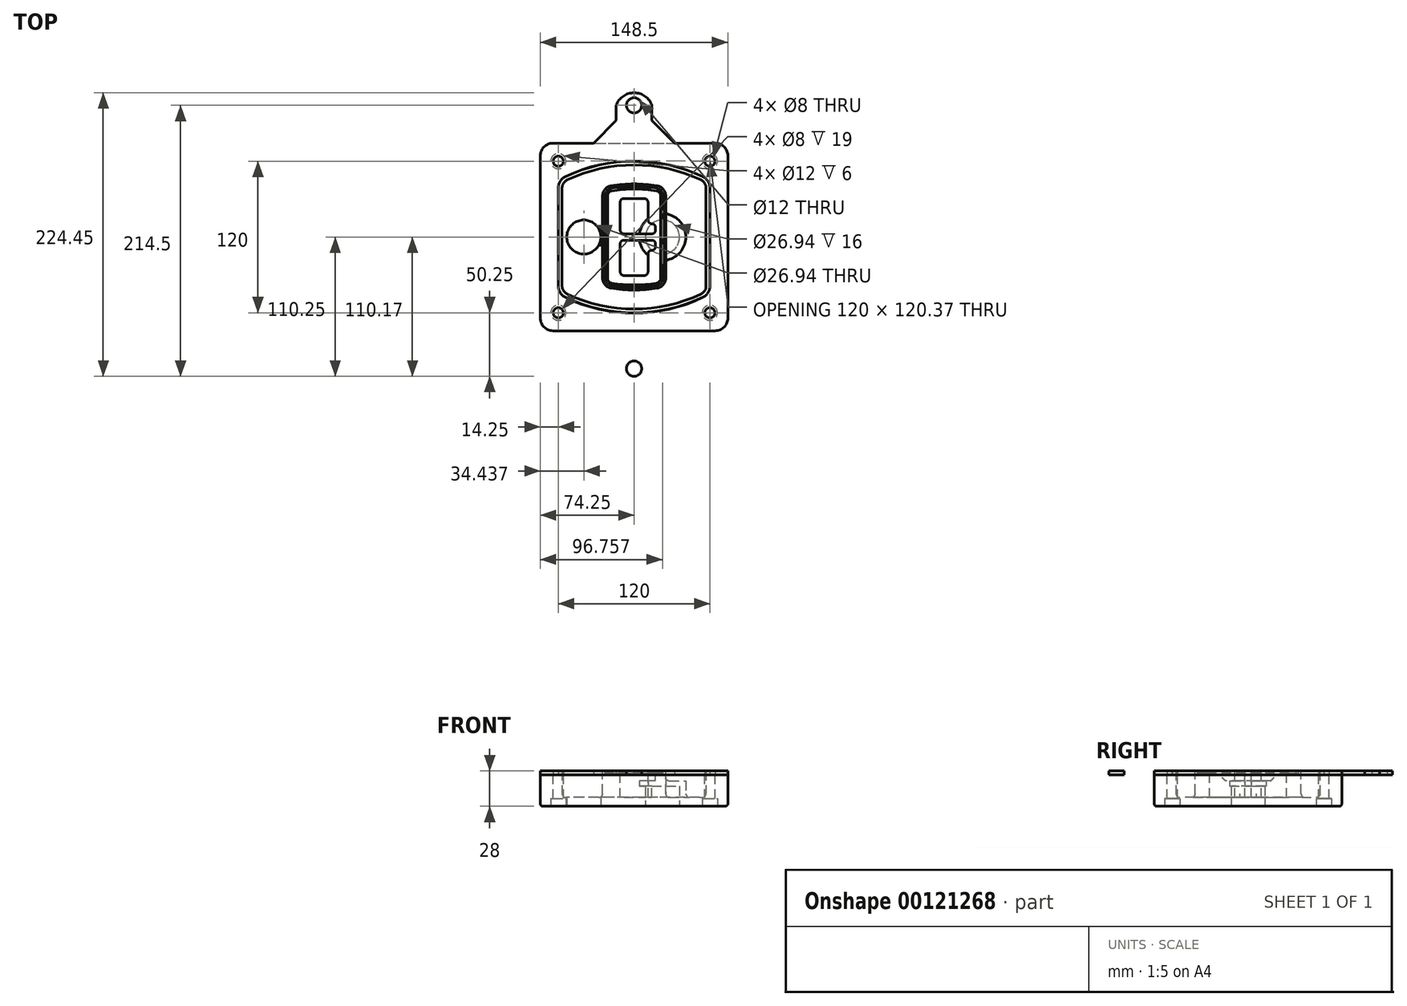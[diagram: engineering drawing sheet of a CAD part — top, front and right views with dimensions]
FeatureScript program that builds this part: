
annotation { "Feature Type Name" : "Feature", "Feature Type Description" : "" }
export const myFeature = defineFeature(function(context is Context, id is Id, definition is map)
    precondition{}
    {
        {
            var Q0;
            Q0=qCreatedBy(makeId("Top.planeOp"),FACE);
            var sketch = newSketch(context, id + "F0", { "sketchPlane" : qUnion([Q0])});
            skPoint(sketch, "E0.rect.middle", {"position": v(0, 0) * mm});
            skLineSegment(sketch, "E1.bottom", {"start": v(-64.25, -74.25) * mm, "end": v(64.25, -74.25) * mm});
            skLineSegment(sketch, "E1.top", {"start": v(-64.25, 74.25) * mm, "end": v(64.25, 74.25) * mm});
            skLineSegment(sketch, "E1.left", {"start": v(-74.25, -64.25) * mm, "end": v(-74.25, 64.25) * mm});
            skLineSegment(sketch, "E1.right", {"start": v(74.25, -64.25) * mm, "end": v(74.25, 64.25) * mm});
            skLineSegment(sketch, "E2", {"start": v(-74.25, 74.25) * mm, "end": v(74.25, -74.25) * mm, "construction": true});
            skLineSegment(sketch, "E3", {"start": v(74.25, 74.25) * mm, "end": v(-74.25, -74.25) * mm, "construction": true});
            skCircle(sketch, "E4", {"center": v(-60, 60) * mm, "radius": 4 * mm});
            skCircle(sketch, "E5", {"center": v(60, 60) * mm, "radius": 4 * mm});
            skCircle(sketch, "E6", {"center": v(60, -60) * mm, "radius": 4 * mm});
            skCircle(sketch, "E7", {"center": v(-60, -60) * mm, "radius": 4 * mm});
            skLineSegment(sketch, "E8", {"start": v(-60, 60) * mm, "end": v(60, 60) * mm, "construction": true});
            skLineSegment(sketch, "E9", {"start": v(60, 60) * mm, "end": v(60, -60) * mm, "construction": true});
            skLineSegment(sketch, "E10", {"start": v(60, -60) * mm, "end": v(-60, -60) * mm, "construction": true});
            skLineSegment(sketch, "E11", {"start": v(-60, -60) * mm, "end": v(-60, 60) * mm, "construction": true});
            skLineSegment(sketch, "E12", {"start": v(-60, 38.83) * mm, "end": v(-60, -38.83) * mm});
            skLineSegment(sketch, "E13", {"start": v(60, 38.83) * mm, "end": v(60, -38.83) * mm});
            skArc(sketch, "E14", {"start": v(54.26, 47.88) * mm, "mid": v(0, 60) * mm, "end": v(-54.26, 47.88) * mm});
            skArc(sketch, "E15", {"start": v(-54.26, -47.88) * mm, "mid": v(0, -60) * mm, "end": v(54.26, -47.88) * mm});
            skLineSegment(sketch, "E16", {"start": v(-60, 0) * mm, "end": v(60, 0) * mm, "construction": true});
            skPoint(sketch, "E17.visualSharp", {"position": v(-60, -45) * mm});
            skArc(sketch, "E17.filletArc", {"start": v(-60, -38.83) * mm, "mid": v(-58.44, -44.2) * mm, "end": v(-54.26, -47.88) * mm});
            skPoint(sketch, "E18.visualSharp", {"position": v(-60, 45) * mm});
            skArc(sketch, "E18.filletArc", {"start": v(-54.26, 47.88) * mm, "mid": v(-58.44, 44.2) * mm, "end": v(-60, 38.83) * mm});
            skPoint(sketch, "E19.visualSharp", {"position": v(60, 45) * mm});
            skArc(sketch, "E19.filletArc", {"start": v(60, 38.83) * mm, "mid": v(58.44, 44.2) * mm, "end": v(54.26, 47.88) * mm});
            skPoint(sketch, "E20.visualSharp", {"position": v(60, -45) * mm});
            skArc(sketch, "E20.filletArc", {"start": v(54.26, -47.88) * mm, "mid": v(58.44, -44.2) * mm, "end": v(60, -38.83) * mm});
            skPoint(sketch, "E21.visualSharp", {"position": v(-74.25, 74.25) * mm});
            skArc(sketch, "E21.filletArc", {"start": v(-64.25, 74.25) * mm, "mid": v(-71.32, 71.32) * mm, "end": v(-74.25, 64.25) * mm});
            skPoint(sketch, "E22.visualSharp", {"position": v(74.25, 74.25) * mm});
            skArc(sketch, "E22.filletArc", {"start": v(74.25, 64.25) * mm, "mid": v(71.32, 71.32) * mm, "end": v(64.25, 74.25) * mm});
            skPoint(sketch, "E23.visualSharp", {"position": v(74.25, -74.25) * mm});
            skArc(sketch, "E23.filletArc", {"start": v(64.25, -74.25) * mm, "mid": v(71.32, -71.32) * mm, "end": v(74.25, -64.25) * mm});
            skPoint(sketch, "E24.visualSharp", {"position": v(-74.25, -74.25) * mm});
            skArc(sketch, "E24.filletArc", {"start": v(-74.25, -64.25) * mm, "mid": v(-71.32, -71.32) * mm, "end": v(-64.25, -74.25) * mm});
            skArc(sketch, "E25.0", {"start": v(57, 38.83) * mm, "mid": v(55.9, 42.58) * mm, "end": v(52.98, 45.17) * mm});
            skLineSegment(sketch, "E25.1", {"start": v(57, 38.83) * mm, "end": v(57, -38.83) * mm});
            skArc(sketch, "E25.2", {"start": v(52.98, -45.17) * mm, "mid": v(55.9, -42.58) * mm, "end": v(57, -38.83) * mm});
            skArc(sketch, "E25.3", {"start": v(-52.98, -45.17) * mm, "mid": v(0, -57) * mm, "end": v(52.98, -45.17) * mm});
            skArc(sketch, "E25.4", {"start": v(-57, -38.83) * mm, "mid": v(-55.9, -42.58) * mm, "end": v(-52.98, -45.17) * mm});
            skArc(sketch, "E25.5", {"start": v(52.98, 45.17) * mm, "mid": v(0, 57) * mm, "end": v(-52.98, 45.17) * mm});
            skLineSegment(sketch, "E25.6", {"start": v(-57, 38.83) * mm, "end": v(-57, -38.83) * mm});
            skArc(sketch, "E25.7", {"start": v(-52.98, 45.17) * mm, "mid": v(-55.9, 42.58) * mm, "end": v(-57, 38.83) * mm});
            skArc(sketch, "E26.0", {"start": v(-55.96, 51.5) * mm, "mid": v(-61.82, 46.33) * mm, "end": v(-64, 38.83) * mm});
            skArc(sketch, "E26.1", {"start": v(55.96, 51.5) * mm, "mid": v(0, 64) * mm, "end": v(-55.96, 51.5) * mm});
            skArc(sketch, "E26.2", {"start": v(64, 38.83) * mm, "mid": v(61.82, 46.33) * mm, "end": v(55.96, 51.5) * mm});
            skLineSegment(sketch, "E26.3", {"start": v(64, 38.83) * mm, "end": v(64, -38.83) * mm});
            skArc(sketch, "E26.4", {"start": v(55.96, -51.5) * mm, "mid": v(61.82, -46.33) * mm, "end": v(64, -38.83) * mm});
            skLineSegment(sketch, "E26.5", {"start": v(-64, 38.83) * mm, "end": v(-64, -38.83) * mm});
            skArc(sketch, "E26.6", {"start": v(-55.96, -51.5) * mm, "mid": v(0, -64) * mm, "end": v(55.96, -51.5) * mm});
            skArc(sketch, "E26.7", {"start": v(-64, -38.83) * mm, "mid": v(-61.82, -46.33) * mm, "end": v(-55.96, -51.5) * mm});
            skSolve(sketch);
        }
        {
            var Q0;
            Q0=makeQuery(id+"F0.imprint","IMPRINT",FACE,{"disambiguationData":[TD([[makeQuery(id+"F0.imprint","IMPRINT",EDGE,{"derivedFrom":sQuery(id+"F0.wireOp",EDGE,"E1.bottom")}),1.0]])]});
            var Q1;
            Q1=makeQuery(id+"F0.imprint","IMPRINT",FACE,{"disambiguationData":[TD([[makeQuery(id+"F0.imprint","IMPRINT",EDGE,{"derivedFrom":sQuery(id+"F0.wireOp",EDGE,"E12")}),1.0]])]});
            var Q2;
            Q2=makeQuery(id+"F0.imprint","IMPRINT",FACE,{"disambiguationData":[TD([[makeQuery(id+"F0.imprint","IMPRINT",EDGE,{"derivedFrom":sQuery(id+"F0.wireOp",EDGE,"E25.0")}),1.0]])]});
            var Q3;
            Q3=makeQuery(id+"F0.imprint","IMPRINT",FACE,{"disambiguationData":[TD([[makeQuery(id+"F0.imprint","IMPRINT",EDGE,{"derivedFrom":sQuery(id+"F0.wireOp",EDGE,"E12")}),-1.0]])]});
            extrude(context, id + "F1", {"entities" : qUnion([Q0, Q1, Q2, Q3]), "oppositeDirection" : true, "depth" : 25 * mm});
        }
        {
            var Q0;
            Q0=makeQuery(id+"F0.imprint","IMPRINT",FACE,{"disambiguationData":[TD([[makeQuery(id+"F0.imprint","IMPRINT",EDGE,{"derivedFrom":sQuery(id+"F0.wireOp",EDGE,"E12")}),1.0]])]});
            extrude(context, id + "F2", {"entities" : qUnion([Q0]), "operationType" : NewBodyOperationType.ADD, "depth" : 3 * mm});
        }
        {
            var Q0;
            Q0=makeQuery(id+"F0.imprint","IMPRINT",FACE,{"disambiguationData":[TD([[makeQuery(id+"F0.imprint","IMPRINT",EDGE,{"derivedFrom":sQuery(id+"F0.wireOp",EDGE,"E25.0")}),1.0]])]});
            extrude(context, id + "F3", {"entities" : qUnion([Q0]), "operationType" : NewBodyOperationType.REMOVE, "oppositeDirection" : true, "depth" : 18 * mm});
        }
        {
            var Q0;
            Q0=makeQuery(id+"F2.opExtrude","CAP_FACE",FACE,{"disambiguationData":[OSD([sQuery(id+"F0.wireOp",EDGE,"E12"),sQuery(id+"F0.wireOp",EDGE,"E13"),sQuery(id+"F0.wireOp",EDGE,"E14"),sQuery(id+"F0.wireOp",EDGE,"E15"),sQuery(id+"F0.wireOp",EDGE,"E17.filletArc"),sQuery(id+"F0.wireOp",EDGE,"E18.filletArc"),sQuery(id+"F0.wireOp",EDGE,"E19.filletArc"),sQuery(id+"F0.wireOp",EDGE,"E20.filletArc"),sQuery(id+"F0.wireOp",EDGE,"E25.0"),sQuery(id+"F0.wireOp",EDGE,"E25.1"),sQuery(id+"F0.wireOp",EDGE,"E25.2"),sQuery(id+"F0.wireOp",EDGE,"E25.3"),sQuery(id+"F0.wireOp",EDGE,"E25.4"),sQuery(id+"F0.wireOp",EDGE,"E25.5"),sQuery(id+"F0.wireOp",EDGE,"E25.6"),sQuery(id+"F0.wireOp",EDGE,"E25.7")])],"isStart":false});
            var sketch = newSketch(context, id + "F4", { "sketchPlane" : qUnion([Q0])});
            skArc(sketch, "E27.0", {"start": v(-18.34, -40.45) * mm, "mid": v(0, -42) * mm, "end": v(18.34, -40.45) * mm});
            skArc(sketch, "E28.0", {"start": v(18.34, 40.45) * mm, "mid": v(0, 42) * mm, "end": v(-18.34, 40.45) * mm});
            skLineSegment(sketch, "E29", {"start": v(-25, 32.57) * mm, "end": v(-25, -32.57) * mm});
            skLineSegment(sketch, "E30", {"start": v(25, 32.57) * mm, "end": v(25, -32.57) * mm});
            skLineSegment(sketch, "E31", {"start": v(-25, 39.1) * mm, "end": v(25, 39.1) * mm, "construction": true});
            skLineSegment(sketch, "E32", {"start": v(-25, -39.1) * mm, "end": v(25, -39.1) * mm, "construction": true});
            skPoint(sketch, "E33.visualSharp", {"position": v(-25, 39.1) * mm});
            skArc(sketch, "E33.filletArc", {"start": v(-18.34, 40.45) * mm, "mid": v(-23.11, 37.73) * mm, "end": v(-25, 32.57) * mm});
            skPoint(sketch, "E34.visualSharp", {"position": v(25, 39.1) * mm});
            skArc(sketch, "E34.filletArc", {"start": v(25, 32.57) * mm, "mid": v(23.11, 37.73) * mm, "end": v(18.34, 40.45) * mm});
            skPoint(sketch, "E35.visualSharp", {"position": v(25, -39.1) * mm});
            skArc(sketch, "E35.filletArc", {"start": v(18.34, -40.45) * mm, "mid": v(23.11, -37.73) * mm, "end": v(25, -32.57) * mm});
            skPoint(sketch, "E36.visualSharp", {"position": v(-25, -39.1) * mm});
            skArc(sketch, "E36.filletArc", {"start": v(-25, -32.57) * mm, "mid": v(-23.11, -37.73) * mm, "end": v(-18.34, -40.45) * mm});
            skArc(sketch, "E37.0", {"start": v(52.98, 45.17) * mm, "mid": v(0, 57) * mm, "end": v(-52.98, 45.17) * mm});
            skArc(sketch, "E37.1", {"start": v(-52.98, 45.17) * mm, "mid": v(-55.9, 42.58) * mm, "end": v(-57, 38.83) * mm});
            skLineSegment(sketch, "E37.2", {"start": v(-57, 38.83) * mm, "end": v(-57, -38.83) * mm});
            skArc(sketch, "E37.3", {"start": v(-57, -38.83) * mm, "mid": v(-55.9, -42.58) * mm, "end": v(-52.98, -45.17) * mm});
            skArc(sketch, "E37.4", {"start": v(-52.98, -45.17) * mm, "mid": v(0, -57) * mm, "end": v(52.98, -45.17) * mm});
            skArc(sketch, "E37.5", {"start": v(52.98, -45.17) * mm, "mid": v(55.9, -42.58) * mm, "end": v(57, -38.83) * mm});
            skLineSegment(sketch, "E37.6", {"start": v(57, 38.83) * mm, "end": v(57, -38.83) * mm});
            skArc(sketch, "E37.7", {"start": v(57, 38.83) * mm, "mid": v(55.9, 42.58) * mm, "end": v(52.98, 45.17) * mm});
            skLineSegment(sketch, "E38.0", {"start": v(23, 32.57) * mm, "end": v(23, -32.57) * mm});
            skArc(sketch, "E38.1", {"start": v(18, -38.48) * mm, "mid": v(21.58, -36.44) * mm, "end": v(23, -32.57) * mm});
            skArc(sketch, "E38.2", {"start": v(-18, -38.48) * mm, "mid": v(0, -40) * mm, "end": v(18, -38.48) * mm});
            skArc(sketch, "E38.3", {"start": v(-23, -32.57) * mm, "mid": v(-21.58, -36.44) * mm, "end": v(-18, -38.48) * mm});
            skLineSegment(sketch, "E38.4", {"start": v(-23, 32.57) * mm, "end": v(-23, -32.57) * mm});
            skArc(sketch, "E38.5", {"start": v(23, 32.57) * mm, "mid": v(21.58, 36.44) * mm, "end": v(18, 38.48) * mm});
            skArc(sketch, "E38.6", {"start": v(-18, 38.48) * mm, "mid": v(-21.58, 36.44) * mm, "end": v(-23, 32.57) * mm});
            skArc(sketch, "E38.7", {"start": v(18, 38.48) * mm, "mid": v(0, 40) * mm, "end": v(-18, 38.48) * mm});
            skArc(sketch, "E39.0", {"start": v(21, 32.57) * mm, "mid": v(20.06, 35.15) * mm, "end": v(17.67, 36.5) * mm});
            skLineSegment(sketch, "E39.1", {"start": v(21, 32.57) * mm, "end": v(21, -32.57) * mm});
            skArc(sketch, "E39.2", {"start": v(17.67, -36.5) * mm, "mid": v(20.06, -35.15) * mm, "end": v(21, -32.57) * mm});
            skArc(sketch, "E39.3", {"start": v(-17.67, -36.5) * mm, "mid": v(0, -38) * mm, "end": v(17.67, -36.5) * mm});
            skArc(sketch, "E39.4", {"start": v(-21, -32.57) * mm, "mid": v(-20.06, -35.15) * mm, "end": v(-17.67, -36.5) * mm});
            skArc(sketch, "E39.5", {"start": v(17.67, 36.5) * mm, "mid": v(0, 38) * mm, "end": v(-17.67, 36.5) * mm});
            skLineSegment(sketch, "E39.6", {"start": v(-21, 32.57) * mm, "end": v(-21, -32.57) * mm});
            skArc(sketch, "E39.7", {"start": v(-17.67, 36.5) * mm, "mid": v(-20.06, 35.15) * mm, "end": v(-21, 32.57) * mm});
            skLineSegment(sketch, "E40", {"start": v(-25, 0) * mm, "end": v(25, 0) * mm, "construction": true});
            skLineSegment(sketch, "E41", {"start": v(-11, 5.5) * mm, "end": v(-11, 27.5) * mm});
            skLineSegment(sketch, "E42", {"start": v(-8, 30.5) * mm, "end": v(8, 30.5) * mm});
            skLineSegment(sketch, "E43", {"start": v(11, 27.5) * mm, "end": v(11, 13.5) * mm});
            skLineSegment(sketch, "E44", {"start": v(14, 10.5) * mm, "end": v(14, 10.5) * mm});
            skLineSegment(sketch, "E45", {"start": v(17, 7.5) * mm, "end": v(17, 5.5) * mm});
            skLineSegment(sketch, "E46", {"start": v(14, 2.5) * mm, "end": v(-8, 2.5) * mm});
            skPoint(sketch, "E47.visualSharp", {"position": v(-11, 30.5) * mm});
            skArc(sketch, "E47.filletArc", {"start": v(-8, 30.5) * mm, "mid": v(-10.12, 29.62) * mm, "end": v(-11, 27.5) * mm});
            skPoint(sketch, "E48.visualSharp", {"position": v(11, 30.5) * mm});
            skArc(sketch, "E48.filletArc", {"start": v(11, 27.5) * mm, "mid": v(10.12, 29.62) * mm, "end": v(8, 30.5) * mm});
            skPoint(sketch, "E49.visualSharp", {"position": v(11, 10.5) * mm});
            skArc(sketch, "E49.filletArc", {"start": v(11, 13.5) * mm, "mid": v(11.88, 11.38) * mm, "end": v(14, 10.5) * mm});
            skPoint(sketch, "E50.visualSharp", {"position": v(17, 10.5) * mm});
            skArc(sketch, "E50.filletArc", {"start": v(17, 7.5) * mm, "mid": v(16.12, 9.62) * mm, "end": v(14, 10.5) * mm});
            skPoint(sketch, "E51.visualSharp", {"position": v(17, 2.5) * mm});
            skArc(sketch, "E51.filletArc", {"start": v(14, 2.5) * mm, "mid": v(16.12, 3.38) * mm, "end": v(17, 5.5) * mm});
            skPoint(sketch, "E52.visualSharp", {"position": v(-11, 2.5) * mm});
            skArc(sketch, "E52.filletArc", {"start": v(-11, 5.5) * mm, "mid": v(-10.12, 3.38) * mm, "end": v(-8, 2.5) * mm});
            skLineSegment(sketch, "E53.0.MirrorCS", {"start": v(14, -2.5) * mm, "end": v(-8, -2.5) * mm});
            skArc(sketch, "E54.0.MirrorCS", {"start": v(-11, -5.5) * mm, "mid": v(-10.12, -3.38) * mm, "end": v(-8, -2.5) * mm});
            skLineSegment(sketch, "E55.0.MirrorCS", {"start": v(-11, -5.5) * mm, "end": v(-11, -27.5) * mm});
            skArc(sketch, "E56.0.MirrorCS", {"start": v(-8, -30.5) * mm, "mid": v(-10.12, -29.62) * mm, "end": v(-11, -27.5) * mm});
            skLineSegment(sketch, "E57.0.MirrorCS", {"start": v(-8, -30.5) * mm, "end": v(8, -30.5) * mm});
            skArc(sketch, "E58.0.MirrorCS", {"start": v(11, -27.5) * mm, "mid": v(10.12, -29.62) * mm, "end": v(8, -30.5) * mm});
            skLineSegment(sketch, "E59.0.MirrorCS", {"start": v(11, -27.5) * mm, "end": v(11, -13.5) * mm});
            skArc(sketch, "E60.0.MirrorCS", {"start": v(11, -13.5) * mm, "mid": v(11.88, -11.38) * mm, "end": v(14, -10.5) * mm});
            skArc(sketch, "E61.0.MirrorCS", {"start": v(17, -7.5) * mm, "mid": v(16.12, -9.62) * mm, "end": v(14, -10.5) * mm});
            skLineSegment(sketch, "E62.0.MirrorCS", {"start": v(17, -7.5) * mm, "end": v(17, -5.5) * mm});
            skArc(sketch, "E63.0.MirrorCS", {"start": v(14, -2.5) * mm, "mid": v(16.12, -3.38) * mm, "end": v(17, -5.5) * mm});
            skSolve(sketch);
        }
        {
            var Q0;
            Q0=makeQuery(id+"F4.imprint","IMPRINT",FACE,{"disambiguationData":[TD([[makeQuery(id+"F4.imprint","IMPRINT",EDGE,{"derivedFrom":sQuery(id+"F4.wireOp",EDGE,"E27.0")}),1.0]])]});
            var Q1;
            Q1=makeQuery(id+"F4.imprint","IMPRINT",FACE,{"disambiguationData":[TD([[makeQuery(id+"F4.imprint","IMPRINT",EDGE,{"derivedFrom":sQuery(id+"F4.wireOp",EDGE,"E38.0")}),-1.0]])]});
            var Q2;
            Q2=makeQuery(id+"F4.imprint","IMPRINT",FACE,{"disambiguationData":[TD([[makeQuery(id+"F4.imprint","IMPRINT",EDGE,{"derivedFrom":sQuery(id+"F4.wireOp",EDGE,"E39.0")}),1.0]])]});
            extrude(context, id + "F5", {"entities" : qUnion([Q0, Q1, Q2]), "operationType" : NewBodyOperationType.ADD, "endBound" : BoundingType.UP_TO_NEXT, "oppositeDirection" : true, "depth" : 25 * mm});
        }
        {
            var Q0;
            Q0=makeQuery(id+"F4.imprint","IMPRINT",FACE,{"disambiguationData":[TD([[makeQuery(id+"F4.imprint","IMPRINT",EDGE,{"derivedFrom":sQuery(id+"F4.wireOp",EDGE,"E38.0")}),-1.0]])]});
            extrude(context, id + "F6", {"entities" : qUnion([Q0]), "operationType" : NewBodyOperationType.REMOVE, "oppositeDirection" : true, "depth" : 2 * mm});
        }
        {
            var Q0;
            Q0=makeQuery(id+"F1.opExtrude","CAP_FACE",FACE,{"disambiguationData":[OSD([sQuery(id+"F0.wireOp",EDGE,"E1.bottom"),sQuery(id+"F0.wireOp",EDGE,"E1.top"),sQuery(id+"F0.wireOp",EDGE,"E1.left"),sQuery(id+"F0.wireOp",EDGE,"E1.right"),sQuery(id+"F0.wireOp",EDGE,"E4"),sQuery(id+"F0.wireOp",EDGE,"E5"),sQuery(id+"F0.wireOp",EDGE,"E6"),sQuery(id+"F0.wireOp",EDGE,"E7"),sQuery(id+"F0.wireOp",EDGE,"E21.filletArc"),sQuery(id+"F0.wireOp",EDGE,"E22.filletArc"),sQuery(id+"F0.wireOp",EDGE,"E23.filletArc"),sQuery(id+"F0.wireOp",EDGE,"E24.filletArc")])],"isStart":false});
            var sketch = newSketch(context, id + "F7", { "sketchPlane" : qUnion([Q0])});
            skCircle(sketch, "E64", {"center": v(22.5, 0) * mm, "radius": 13.47 * mm});
            skCircle(sketch, "E65", {"center": v(-39.81, 0) * mm, "radius": 13.47 * mm});
            skLineSegment(sketch, "E66", {"start": v(74.25, 0) * mm, "end": v(-74.25, 0) * mm});
            skCircle(sketch, "E67", {"center": v(22.5, 0) * mm, "radius": 18.47 * mm});
            skCircle(sketch, "E68", {"center": v(60, -60) * mm, "radius": 6 * mm});
            skCircle(sketch, "E69", {"center": v(-60, -60) * mm, "radius": 6 * mm});
            skCircle(sketch, "E70", {"center": v(-60, 60) * mm, "radius": 6 * mm});
            skCircle(sketch, "E71", {"center": v(60, 60) * mm, "radius": 6 * mm});
            skSolve(sketch);
        }
        {
            var Q0;
            {var subQ1=sQuery(id+"F7.wireOp",EDGE,"E66");var subQ4=sQuery(id+"F7.wireOp",EDGE,"E64");var subQ6=makeQuery(id+"F7.imprint","INTERSECT",VERTEX,{"disambiguationData":[OD(0.0)],"derivedFrom":[subQ4,subQ1]});Q0=makeQuery(id+"F7.imprint","IMPRINT",FACE,{"disambiguationData":[TD([[makeQuery(id+"F7.imprint","IMPRINT",EDGE,{"disambiguationData":[TD([[subQ6,-1.0]])],"derivedFrom":subQ4}),-1.0]])]});}
            var Q1;
            {var subQ0=sQuery(id+"F7.wireOp",EDGE,"E66");var subQ1=sQuery(id+"F7.wireOp",EDGE,"E64");var subQ3=makeQuery(id+"F7.imprint","INTERSECT",VERTEX,{"disambiguationData":[OD(0.0)],"derivedFrom":[subQ1,subQ0]});Q1=makeQuery(id+"F7.imprint","IMPRINT",FACE,{"disambiguationData":[TD([[makeQuery(id+"F7.imprint","IMPRINT",EDGE,{"disambiguationData":[TD([[subQ3,-1.0]])],"derivedFrom":subQ1}),1.0]])]});}
            var Q2;
            {var subQ0=sQuery(id+"F7.wireOp",EDGE,"E66");var subQ1=sQuery(id+"F7.wireOp",EDGE,"E64");var subQ3=makeQuery(id+"F7.imprint","INTERSECT",VERTEX,{"disambiguationData":[OD(0.0)],"derivedFrom":[subQ1,subQ0]});Q2=makeQuery(id+"F7.imprint","IMPRINT",FACE,{"disambiguationData":[TD([[makeQuery(id+"F7.imprint","IMPRINT",EDGE,{"disambiguationData":[TD([[subQ3,1.0]])],"derivedFrom":subQ1}),1.0]])]});}
            var Q3;
            {var subQ1=sQuery(id+"F7.wireOp",EDGE,"E66");var subQ4=sQuery(id+"F7.wireOp",EDGE,"E64");var subQ6=makeQuery(id+"F7.imprint","INTERSECT",VERTEX,{"disambiguationData":[OD(0.0)],"derivedFrom":[subQ4,subQ1]});Q3=makeQuery(id+"F7.imprint","IMPRINT",FACE,{"disambiguationData":[TD([[makeQuery(id+"F7.imprint","IMPRINT",EDGE,{"disambiguationData":[TD([[subQ6,1.0]])],"derivedFrom":subQ4}),-1.0]])]});}
            extrude(context, id + "F8", {"entities" : qUnion([Q0, Q1, Q2, Q3]), "operationType" : NewBodyOperationType.ADD, "oppositeDirection" : true, "depth" : 20 * mm});
        }
        {
            var Q0;
            {var subQ0=sQuery(id+"F7.wireOp",EDGE,"E66");var subQ1=sQuery(id+"F7.wireOp",EDGE,"E64");var subQ3=makeQuery(id+"F7.imprint","INTERSECT",VERTEX,{"disambiguationData":[OD(0.0)],"derivedFrom":[subQ1,subQ0]});Q0=makeQuery(id+"F7.imprint","IMPRINT",FACE,{"disambiguationData":[TD([[makeQuery(id+"F7.imprint","IMPRINT",EDGE,{"disambiguationData":[TD([[subQ3,-1.0]])],"derivedFrom":subQ1}),1.0]])]});}
            var Q1;
            {var subQ0=sQuery(id+"F7.wireOp",EDGE,"E66");var subQ1=sQuery(id+"F7.wireOp",EDGE,"E64");var subQ3=makeQuery(id+"F7.imprint","INTERSECT",VERTEX,{"disambiguationData":[OD(0.0)],"derivedFrom":[subQ1,subQ0]});Q1=makeQuery(id+"F7.imprint","IMPRINT",FACE,{"disambiguationData":[TD([[makeQuery(id+"F7.imprint","IMPRINT",EDGE,{"disambiguationData":[TD([[subQ3,1.0]])],"derivedFrom":subQ1}),1.0]])]});}
            extrude(context, id + "F9", {"entities" : qUnion([Q0, Q1]), "operationType" : NewBodyOperationType.REMOVE, "oppositeDirection" : true, "depth" : 16 * mm});
        }
        {
            var Q0;
            {var subQ0=sQuery(id+"F7.wireOp",EDGE,"E66");var subQ1=sQuery(id+"F7.wireOp",EDGE,"E65");var subQ3=makeQuery(id+"F7.imprint","INTERSECT",VERTEX,{"disambiguationData":[OD(0.0)],"derivedFrom":[subQ1,subQ0]});Q0=makeQuery(id+"F7.imprint","IMPRINT",FACE,{"disambiguationData":[TD([[makeQuery(id+"F7.imprint","IMPRINT",EDGE,{"disambiguationData":[TD([[subQ3,-1.0]])],"derivedFrom":subQ1}),1.0]])]});}
            var Q1;
            {var subQ0=sQuery(id+"F7.wireOp",EDGE,"E66");var subQ1=sQuery(id+"F7.wireOp",EDGE,"E65");var subQ3=makeQuery(id+"F7.imprint","INTERSECT",VERTEX,{"disambiguationData":[OD(0.0)],"derivedFrom":[subQ1,subQ0]});Q1=makeQuery(id+"F7.imprint","IMPRINT",FACE,{"disambiguationData":[TD([[makeQuery(id+"F7.imprint","IMPRINT",EDGE,{"disambiguationData":[TD([[subQ3,1.0]])],"derivedFrom":subQ1}),1.0]])]});}
            extrude(context, id + "F10", {"entities" : qUnion([Q0, Q1]), "operationType" : NewBodyOperationType.REMOVE, "oppositeDirection" : true, "depth" : 25 * mm});
        }
        {
            var Q0;
            Q0=makeQuery(id+"F7.imprint","IMPRINT",FACE,{"disambiguationData":[TD([[makeQuery(id+"F7.imprint","IMPRINT",EDGE,{"derivedFrom":sQuery(id+"F7.wireOp",EDGE,"E68")}),1.0]])]});
            var Q1;
            Q1=makeQuery(id+"F7.imprint","IMPRINT",FACE,{"disambiguationData":[TD([[makeQuery(id+"F7.imprint","IMPRINT",EDGE,{"derivedFrom":makeQuery(id+"F1.opExtrude","CAP_EDGE",EDGE,{"disambiguationData":[OSD([sQuery(id+"F0.wireOp",EDGE,"E5")])],"isStart":false})}),-1.0]])]});
            var Q2;
            Q2=makeQuery(id+"F7.imprint","IMPRINT",FACE,{"disambiguationData":[TD([[makeQuery(id+"F7.imprint","IMPRINT",EDGE,{"derivedFrom":sQuery(id+"F7.wireOp",EDGE,"E69")}),1.0]])]});
            var Q3;
            Q3=makeQuery(id+"F7.imprint","IMPRINT",FACE,{"disambiguationData":[TD([[makeQuery(id+"F7.imprint","IMPRINT",EDGE,{"derivedFrom":makeQuery(id+"F1.opExtrude","CAP_EDGE",EDGE,{"disambiguationData":[OSD([sQuery(id+"F0.wireOp",EDGE,"E4")])],"isStart":false})}),-1.0]])]});
            var Q4;
            Q4=makeQuery(id+"F7.imprint","IMPRINT",FACE,{"disambiguationData":[TD([[makeQuery(id+"F7.imprint","IMPRINT",EDGE,{"derivedFrom":sQuery(id+"F7.wireOp",EDGE,"E70")}),1.0]])]});
            var Q5;
            Q5=makeQuery(id+"F7.imprint","IMPRINT",FACE,{"disambiguationData":[TD([[makeQuery(id+"F7.imprint","IMPRINT",EDGE,{"derivedFrom":makeQuery(id+"F1.opExtrude","CAP_EDGE",EDGE,{"disambiguationData":[OSD([sQuery(id+"F0.wireOp",EDGE,"E7")])],"isStart":false})}),-1.0]])]});
            var Q6;
            Q6=makeQuery(id+"F7.imprint","IMPRINT",FACE,{"disambiguationData":[TD([[makeQuery(id+"F7.imprint","IMPRINT",EDGE,{"derivedFrom":sQuery(id+"F7.wireOp",EDGE,"E71")}),1.0]])]});
            var Q7;
            Q7=makeQuery(id+"F7.imprint","IMPRINT",FACE,{"disambiguationData":[TD([[makeQuery(id+"F7.imprint","IMPRINT",EDGE,{"derivedFrom":makeQuery(id+"F1.opExtrude","CAP_EDGE",EDGE,{"disambiguationData":[OSD([sQuery(id+"F0.wireOp",EDGE,"E6")])],"isStart":false})}),-1.0]])]});
            extrude(context, id + "F11", {"entities" : qUnion([Q0, Q1, Q2, Q3, Q4, Q5, Q6, Q7]), "operationType" : NewBodyOperationType.REMOVE, "oppositeDirection" : true, "depth" : 6 * mm});
        }
        {
            var Q0;
            Q0=makeQuery(id+"F9.boolean.opBoolean","COPY",FACE,{"derivedFrom":makeQuery(id+"F9.opExtrude","CAP_FACE",FACE,{"disambiguationData":[OSD([sQuery(id+"F7.wireOp",EDGE,"E64")])],"isStart":false})});
            var sketch = newSketch(context, id + "F12", { "sketchPlane" : qUnion([Q0])});
            skArc(sketch, "E72.0", {"start": v(11, 14.45) * mm, "mid": v(6.45, 9.13) * mm, "end": v(4.2, 2.5) * mm});
            skArc(sketch, "E72.1", {"start": v(4.2, -2.5) * mm, "mid": v(6.45, -9.13) * mm, "end": v(11, -14.45) * mm});
            skLineSegment(sketch, "E73", {"start": v(4.2, -2.5) * mm, "end": v(14, -2.5) * mm});
            skLineSegment(sketch, "E74.0", {"start": v(14, 2.5) * mm, "end": v(4.2, 2.5) * mm});
            skArc(sketch, "E74.1", {"start": v(14, 2.5) * mm, "mid": v(16.12, 3.38) * mm, "end": v(17, 5.5) * mm});
            skLineSegment(sketch, "E74.2", {"start": v(17, 7.5) * mm, "end": v(17, 5.5) * mm});
            skArc(sketch, "E74.3", {"start": v(17, 7.5) * mm, "mid": v(16.12, 9.62) * mm, "end": v(14, 10.5) * mm});
            skArc(sketch, "E74.4", {"start": v(11, 13.5) * mm, "mid": v(11.88, 11.38) * mm, "end": v(14, 10.5) * mm});
            skLineSegment(sketch, "E74.5", {"start": v(11, 14.45) * mm, "end": v(11, 13.5) * mm});
            skLineSegment(sketch, "E74.7", {"start": v(14, -2.5) * mm, "end": v(4.2, -2.5) * mm});
            skArc(sketch, "E74.8", {"start": v(14, -2.5) * mm, "mid": v(16.12, -3.38) * mm, "end": v(17, -5.5) * mm});
            skLineSegment(sketch, "E74.9", {"start": v(17, -7.5) * mm, "end": v(17, -5.5) * mm});
            skArc(sketch, "E74.10", {"start": v(17, -7.5) * mm, "mid": v(16.12, -9.62) * mm, "end": v(14, -10.5) * mm});
            skArc(sketch, "E74.11", {"start": v(11, -13.5) * mm, "mid": v(11.88, -11.38) * mm, "end": v(14, -10.5) * mm});
            skLineSegment(sketch, "E74.12", {"start": v(11, -14.45) * mm, "end": v(11, -13.5) * mm});
            skPoint(sketch, "E75.orphan", {"position": v(11, -27.5) * mm});
            skPoint(sketch, "E76.orphan", {"position": v(-8, -2.5) * mm});
            skPoint(sketch, "E77.orphan", {"position": v(-8, 2.5) * mm});
            skPoint(sketch, "E78.orphan", {"position": v(11, 27.5) * mm});
            skSolve(sketch);
        }
        {
            var Q0;
            {var subQ7=sQuery(id+"F12.wireOp",EDGE,"E72.0");var subQ14=sQuery(id+"F12.wireOp",EDGE,"E72.1");var subQ16=sQuery(id+"F12.wireOp",EDGE,"E74.1");var subQ18=sQuery(id+"F12.wireOp",EDGE,"E74.8");Q0=qUnion([makeQuery(id+"F12.imprint","IMPRINT",FACE,{"disambiguationData":[TD([[makeQuery(id+"F12.imprint","IMPRINT",EDGE,{"derivedFrom":subQ7}),1.0]])]}),makeQuery(id+"F12.imprint","IMPRINT",FACE,{"disambiguationData":[TD([[makeQuery(id+"F12.imprint","IMPRINT",EDGE,{"derivedFrom":subQ14}),1.0]])]}),makeQuery(id+"F12.imprint","IMPRINT",FACE,{"disambiguationData":[TD([[makeQuery(id+"F12.imprint","IMPRINT",EDGE,{"derivedFrom":subQ16}),1.0]])]}),makeQuery(id+"F12.imprint","IMPRINT",FACE,{"disambiguationData":[TD([[makeQuery(id+"F12.imprint","IMPRINT",EDGE,{"derivedFrom":subQ18}),-1.0]])]})]);}
            var Q1;
            Q1=makeQuery(id+"F5.boolean.opBoolean","SPLIT",FACE,{"disambiguationData":[TD([makeQuery(id+"F5.opExtrude","SWEPT_FACE",FACE,{"disambiguationData":[OSD([sQuery(id+"F4.wireOp",EDGE,"E41")])]})])],"derivedFrom":makeQuery(id+"F3.boolean.opBoolean","COPY",FACE,{"derivedFrom":makeQuery(id+"F3.opExtrude","CAP_FACE",FACE,{"disambiguationData":[OSD([sQuery(id+"F0.wireOp",EDGE,"E25.0"),sQuery(id+"F0.wireOp",EDGE,"E25.1"),sQuery(id+"F0.wireOp",EDGE,"E25.2"),sQuery(id+"F0.wireOp",EDGE,"E25.3"),sQuery(id+"F0.wireOp",EDGE,"E25.4"),sQuery(id+"F0.wireOp",EDGE,"E25.5"),sQuery(id+"F0.wireOp",EDGE,"E25.6"),sQuery(id+"F0.wireOp",EDGE,"E25.7")])],"isStart":false})})});
            extrude(context, id + "F13", {"entities" : qUnion([Q0]), "operationType" : NewBodyOperationType.REMOVE, "endBound" : BoundingType.UP_TO_SURFACE, "endBoundEntityFace" : qUnion([Q1]), "depth" : 25 * mm});
        }
        {
            var Q0;
            Q0=makeQuery(id+"F3.boolean.opBoolean","COPY",EDGE,{"derivedFrom":makeQuery(id+"F3.opExtrude","CAP_EDGE",EDGE,{"disambiguationData":[OSD([sQuery(id+"F0.wireOp",EDGE,"E25.6")])],"isStart":false})});
            var Q1;
            Q1=makeQuery(id+"F8.boolean.opBoolean","INTERSECT",EDGE,{"derivedFrom":[makeQuery(id+"F5.opExtrude","SWEPT_FACE",FACE,{"disambiguationData":[OSD([sQuery(id+"F4.wireOp",EDGE,"E30")])]}),makeQuery(id+"F8.opExtrude","CAP_FACE",FACE,{"disambiguationData":[OSD([sQuery(id+"F7.wireOp",EDGE,"E67")])],"isStart":false})]});
            var Q2;
            Q2=makeQuery(id+"F8.boolean.opBoolean","INTERSECT",EDGE,{"disambiguationData":[OD(1.0)],"derivedFrom":[makeQuery(id+"F5.opExtrude","SWEPT_FACE",FACE,{"disambiguationData":[OSD([sQuery(id+"F4.wireOp",EDGE,"E30")])]}),makeQuery(id+"F8.opExtrude","SWEPT_FACE",FACE,{"disambiguationData":[OSD([sQuery(id+"F7.wireOp",EDGE,"E67")])]})]});
            var Q3;
            {var subQ0=sQuery(id+"F4.wireOp",EDGE,"E30");Q3=makeQuery(id+"F8.boolean.opBoolean","SPLIT",EDGE,{"disambiguationData":[TD([makeQuery(id+"F5.opExtrude","SWEPT_FACE",FACE,{"disambiguationData":[OSD([sQuery(id+"F4.wireOp",EDGE,"E35.filletArc")])]})])],"derivedFrom":makeQuery(id+"F5.opExtrude","CAP_EDGE",EDGE,{"disambiguationData":[OSD([subQ0])],"isStart":false})});}
            var Q4;
            {var subQ0=sQuery(id+"F0.wireOp",EDGE,"E25.7");var subQ1=sQuery(id+"F0.wireOp",EDGE,"E25.1");var subQ2=sQuery(id+"F0.wireOp",EDGE,"E25.6");var subQ3=sQuery(id+"F0.wireOp",EDGE,"E25.5");var subQ4=sQuery(id+"F0.wireOp",EDGE,"E25.4");var subQ5=sQuery(id+"F0.wireOp",EDGE,"E25.0");var subQ6=sQuery(id+"F0.wireOp",EDGE,"E25.2");var subQ7=sQuery(id+"F0.wireOp",EDGE,"E25.3");Q4=makeQuery(id+"F8.boolean.opBoolean","INTERSECT",EDGE,{"derivedFrom":[makeQuery(id+"F5.boolean.opBoolean","SPLIT",FACE,{"disambiguationData":[TD([makeQuery(id+"F2.opExtrude","SWEPT_FACE",FACE,{"disambiguationData":[OSD([subQ5])]})])],"derivedFrom":makeQuery(id+"F3.boolean.opBoolean","COPY",FACE,{"derivedFrom":makeQuery(id+"F3.opExtrude","CAP_FACE",FACE,{"disambiguationData":[OSD([subQ5,subQ1,subQ6,subQ7,subQ4,subQ3,subQ2,subQ0])],"isStart":false})})}),makeQuery(id+"F8.opExtrude","SWEPT_FACE",FACE,{"disambiguationData":[OSD([sQuery(id+"F7.wireOp",EDGE,"E67")])]})]});}
            var Q5;
            Q5=makeQuery(id+"F8.boolean.opBoolean","INTERSECT",EDGE,{"disambiguationData":[OD(0.0)],"derivedFrom":[makeQuery(id+"F5.opExtrude","SWEPT_FACE",FACE,{"disambiguationData":[OSD([sQuery(id+"F4.wireOp",EDGE,"E30")])]}),makeQuery(id+"F8.opExtrude","SWEPT_FACE",FACE,{"disambiguationData":[OSD([sQuery(id+"F7.wireOp",EDGE,"E67")])]})]});
            fillet(context, id + "F14", {"entities" : qUnion([Q0, Q1, Q2, Q3, Q4, Q5]), "radius" : 3 * mm, "tangentPropagation" : true, "allowEdgeOverflow" : false});
        }
        {
            var Q0;
            Q0=makeQuery(id+"F1.opExtrude","CAP_EDGE",EDGE,{"disambiguationData":[OSD([sQuery(id+"F0.wireOp",EDGE,"E1.bottom")])],"isStart":false});
            fillet(context, id + "F15", {"entities" : qUnion([Q0]), "radius" : 2 * mm, "tangentPropagation" : true, "allowEdgeOverflow" : false});
        }
        {
            var Q0;
            {var subQ0=sQuery(id+"F0.wireOp",EDGE,"E22.filletArc");var subQ1=sQuery(id+"F0.wireOp",EDGE,"E7");var subQ2=sQuery(id+"F0.wireOp",EDGE,"E6");var subQ3=sQuery(id+"F0.wireOp",EDGE,"E5");var subQ4=sQuery(id+"F0.wireOp",EDGE,"E4");var subQ5=sQuery(id+"F0.wireOp",EDGE,"E1.bottom");var subQ6=sQuery(id+"F0.wireOp",EDGE,"E21.filletArc");var subQ7=sQuery(id+"F0.wireOp",EDGE,"E1.top");var subQ8=sQuery(id+"F0.wireOp",EDGE,"E1.left");var subQ9=sQuery(id+"F0.wireOp",EDGE,"E1.right");var subQ10=sQuery(id+"F0.wireOp",EDGE,"E23.filletArc");var subQ11=sQuery(id+"F0.wireOp",EDGE,"E24.filletArc");Q0=makeQuery(id+"F2.boolean.opBoolean","SPLIT",FACE,{"disambiguationData":[TD([makeQuery(id+"F1.opExtrude","SWEPT_FACE",FACE,{"disambiguationData":[OSD([subQ5])]})])],"derivedFrom":makeQuery(id+"F1.opExtrude","CAP_FACE",FACE,{"disambiguationData":[OSD([subQ5,subQ7,subQ8,subQ9,subQ4,subQ3,subQ2,subQ1,subQ6,subQ0,subQ10,subQ11])],"isStart":true})});}
            var sketch = newSketch(context, id + "F16", { "sketchPlane" : qUnion([Q0])});
            skLineSegment(sketch, "E79", {"start": v(-64.25, 74.25) * mm, "end": v(64.25, 74.25) * mm});
            skPoint(sketch, "E80", {"position": v(0, 74.25) * mm});
            skPoint(sketch, "E81", {"position": v(0, 0) * mm});
            skLineSegment(sketch, "E82", {"start": v(0, 74.25) * mm, "end": v(0, 104.25) * mm, "construction": true});
            skCircle(sketch, "E83", {"center": v(0, 104.25) * mm, "radius": 6 * mm});
            skLineSegment(sketch, "E84", {"start": v(0, 74.25) * mm, "end": v(-64.25, 74.25) * mm});
            skLineSegment(sketch, "E85", {"start": v(0, 74.25) * mm, "end": v(64.25, 74.25) * mm});
            skPoint(sketch, "E86", {"position": v(-32.12, 74.25) * mm});
            skPoint(sketch, "E87", {"position": v(32.12, 74.25) * mm});
            skLineSegment(sketch, "E88", {"start": v(-32.12, 74.25) * mm, "end": v(-14.13, 92.25) * mm});
            skLineSegment(sketch, "E89", {"start": v(32.12, 74.25) * mm, "end": v(14.12, 92.25) * mm});
            skLineSegment(sketch, "E90", {"start": v(-14.12, 92.25) * mm, "end": v(-14.12, 104.25) * mm});
            skLineSegment(sketch, "E91", {"start": v(14.12, 92.25) * mm, "end": v(14.12, 104.25) * mm});
            skArc(sketch, "E92", {"start": v(14.12, 104.25) * mm, "mid": v(0, 114.2) * mm, "end": v(-14.12, 104.25) * mm});
            skLineSegment(sketch, "E93", {"start": v(-74.25, 64.25) * mm, "end": v(-74.25, -64.25) * mm});
            skArc(sketch, "E94", {"start": v(-64.25, 74.25) * mm, "mid": v(-71.32, 71.32) * mm, "end": v(-74.25, 64.25) * mm});
            skLineSegment(sketch, "E95", {"start": v(-64.25, -74.25) * mm, "end": v(64.25, -74.25) * mm});
            skLineSegment(sketch, "E96", {"start": v(74.25, 64.25) * mm, "end": v(74.25, -64.25) * mm});
            skArc(sketch, "E97", {"start": v(74.25, 64.25) * mm, "mid": v(71.32, 71.32) * mm, "end": v(64.25, 74.25) * mm});
            skArc(sketch, "E98", {"start": v(64.25, -74.25) * mm, "mid": v(71.32, -71.32) * mm, "end": v(74.25, -64.25) * mm});
            skArc(sketch, "E99", {"start": v(-74.25, -64.25) * mm, "mid": v(-71.32, -71.32) * mm, "end": v(-64.25, -74.25) * mm});
            skPoint(sketch, "E100", {"position": v(-60, 60) * mm});
            skPoint(sketch, "E101", {"position": v(60, 60) * mm});
            skPoint(sketch, "E102", {"position": v(60, -60) * mm});
            skPoint(sketch, "E103", {"position": v(-60, -60) * mm});
            skLineSegment(sketch, "E104", {"start": v(-60, 38.83) * mm, "end": v(-60, -38.83) * mm});
            skLineSegment(sketch, "E105", {"start": v(60, 38.83) * mm, "end": v(60, -38.83) * mm});
            skArc(sketch, "E106", {"start": v(-54.26, 47.88) * mm, "mid": v(-58.44, 44.2) * mm, "end": v(-60, 38.83) * mm});
            skArc(sketch, "E107", {"start": v(54.26, 47.88) * mm, "mid": v(0, 60.1) * mm, "end": v(-54.26, 47.88) * mm});
            skArc(sketch, "E108", {"start": v(60, 38.83) * mm, "mid": v(58.44, 44.2) * mm, "end": v(54.26, 47.88) * mm});
            skArc(sketch, "E109", {"start": v(-54.26, -47.88) * mm, "mid": v(0, -60.26) * mm, "end": v(54.26, -47.88) * mm});
            skArc(sketch, "E110", {"start": v(54.26, -47.88) * mm, "mid": v(58.44, -44.2) * mm, "end": v(60, -38.83) * mm});
            skArc(sketch, "E111", {"start": v(-60, -38.83) * mm, "mid": v(-58.44, -44.2) * mm, "end": v(-54.26, -47.88) * mm});
            skLineSegment(sketch, "E112.MirrorCS", {"start": v(74.25, -69.25) * mm, "end": v(74.25, 59.25) * mm});
            skLineSegment(sketch, "E113.MirrorCS", {"start": v(-74.25, -69.25) * mm, "end": v(-74.25, 59.25) * mm});
            skPoint(sketch, "E114.MirrorP", {"position": v(-60, -65) * mm});
            skPoint(sketch, "E115.MirrorP", {"position": v(60, -65) * mm});
            skLineSegment(sketch, "E116", {"start": v(-74.25, 59.25) * mm, "end": v(-74.25, -64.25) * mm});
            skLineSegment(sketch, "E117", {"start": v(74.25, 59.25) * mm, "end": v(74.25, -64.25) * mm});
            skPoint(sketch, "E118", {"position": v(-74.25, 0) * mm});
            skLineSegment(sketch, "E119", {"start": v(-74.25, 0) * mm, "end": v(74.25, 0) * mm, "construction": true});
            skPoint(sketch, "E120.MirrorP", {"position": v(0, -74.25) * mm});
            skPoint(sketch, "E121.MirrorP", {"position": v(32.12, -74.25) * mm});
            skLineSegment(sketch, "E122.MirrorCS", {"start": v(0, -74.25) * mm, "end": v(0, -104.25) * mm, "construction": true});
            skCircle(sketch, "E123.MirrorC", {"center": v(0, -104.25) * mm, "radius": 6 * mm});
            skLineSegment(sketch, "E124.MirrorCS", {"start": v(-14.12, -92.25) * mm, "end": v(-14.12, -104.25) * mm});
            skLineSegment(sketch, "E125.MirrorCS", {"start": v(14.12, -92.25) * mm, "end": v(14.12, -104.25) * mm});
            skArc(sketch, "E126.MirrorCS", {"start": v(14.12, -104.25) * mm, "mid": v(0, -114.2) * mm, "end": v(-14.12, -104.25) * mm});
            skLineSegment(sketch, "E127.MirrorCS", {"start": v(-32.12, -74.25) * mm, "end": v(-14.13, -92.25) * mm});
            skPoint(sketch, "E128.MirrorP", {"position": v(-32.12, -74.25) * mm});
            skLineSegment(sketch, "E129.MirrorCS", {"start": v(0, -74.25) * mm, "end": v(-64.25, -74.25) * mm});
            skLineSegment(sketch, "E130.MirrorCS", {"start": v(0, -74.25) * mm, "end": v(64.25, -74.25) * mm});
            skLineSegment(sketch, "E131.MirrorCS", {"start": v(32.12, -74.25) * mm, "end": v(14.12, -92.25) * mm});
            skSolve(sketch);
        }
        {
            var Q0;
            Q0=makeQuery(id+"F16.imprint","IMPRINT",FACE,{"disambiguationData":[TD([[makeQuery(id+"F16.imprint","IMPRINT",EDGE,{"derivedFrom":sQuery(id+"F16.wireOp",EDGE,"E93")}),-1.0]])]});
            var Q1;
            Q1=makeQuery(id+"F16.imprint","IMPRINT",FACE,{"disambiguationData":[TD([[makeQuery(id+"F16.imprint","IMPRINT",EDGE,{"derivedFrom":sQuery(id+"F16.wireOp",EDGE,"E83")}),-1.0]])]});
            var Q2;
            Q2=makeQuery(id+"F16.imprint","IMPRINT",FACE,{"disambiguationData":[TD([[makeQuery(id+"F16.imprint","IMPRINT",EDGE,{"derivedFrom":sQuery(id+"F16.wireOp",EDGE,"E123.MirrorC")}),1.0]])]});
            var Q3;
            {var subQ0=sQuery(id+"F4.wireOp",EDGE,"E63.0.MirrorCS");var subQ1=sQuery(id+"F4.wireOp",EDGE,"E62.0.MirrorCS");var subQ2=sQuery(id+"F4.wireOp",EDGE,"E61.0.MirrorCS");var subQ3=sQuery(id+"F4.wireOp",EDGE,"E60.0.MirrorCS");var subQ4=sQuery(id+"F4.wireOp",EDGE,"E59.0.MirrorCS");var subQ5=sQuery(id+"F4.wireOp",EDGE,"E58.0.MirrorCS");var subQ6=sQuery(id+"F4.wireOp",EDGE,"E57.0.MirrorCS");var subQ7=sQuery(id+"F4.wireOp",EDGE,"E56.0.MirrorCS");var subQ8=sQuery(id+"F4.wireOp",EDGE,"E55.0.MirrorCS");var subQ9=sQuery(id+"F4.wireOp",EDGE,"E54.0.MirrorCS");var subQ10=sQuery(id+"F4.wireOp",EDGE,"E53.0.MirrorCS");var subQ11=sQuery(id+"F4.wireOp",EDGE,"E52.filletArc");var subQ12=sQuery(id+"F4.wireOp",EDGE,"E45");var subQ13=sQuery(id+"F4.wireOp",EDGE,"E43");var subQ14=sQuery(id+"F4.wireOp",EDGE,"E42");var subQ15=sQuery(id+"F4.wireOp",EDGE,"E41");var subQ16=sQuery(id+"F4.wireOp",EDGE,"E46");var subQ17=sQuery(id+"F4.wireOp",EDGE,"E47.filletArc");var subQ18=sQuery(id+"F4.wireOp",EDGE,"E48.filletArc");var subQ19=sQuery(id+"F4.wireOp",EDGE,"E49.filletArc");var subQ20=sQuery(id+"F4.wireOp",EDGE,"E50.filletArc");var subQ21=sQuery(id+"F4.wireOp",EDGE,"E51.filletArc");Q3=makeQuery(id+"F6.boolean.opBoolean","SPLIT",FACE,{"disambiguationData":[TD([makeQuery(id+"F5.opExtrude","SWEPT_FACE",FACE,{"disambiguationData":[OSD([subQ15])]})])],"derivedFrom":makeQuery(id+"F5.opExtrude","CAP_FACE",FACE,{"disambiguationData":[OSD([sQuery(id+"F4.wireOp",EDGE,"E27.0"),sQuery(id+"F4.wireOp",EDGE,"E28.0"),sQuery(id+"F4.wireOp",EDGE,"E29"),sQuery(id+"F4.wireOp",EDGE,"E30"),sQuery(id+"F4.wireOp",EDGE,"E33.filletArc"),sQuery(id+"F4.wireOp",EDGE,"E34.filletArc"),sQuery(id+"F4.wireOp",EDGE,"E35.filletArc"),sQuery(id+"F4.wireOp",EDGE,"E36.filletArc"),subQ15,subQ14,subQ13,subQ12,subQ16,subQ17,subQ18,subQ19,subQ20,subQ21,subQ11,subQ10,subQ9,subQ8,subQ7,subQ6,subQ5,subQ4,subQ3,subQ2,subQ1,subQ0])],"isStart":true})});}
            extrude(context, id + "F17", {"entities" : qUnion([Q0, Q1, Q2]), "endBound" : BoundingType.UP_TO_SURFACE, "endBoundEntityFace" : qUnion([Q3]), "depth" : 25 * mm});
        }
    });
